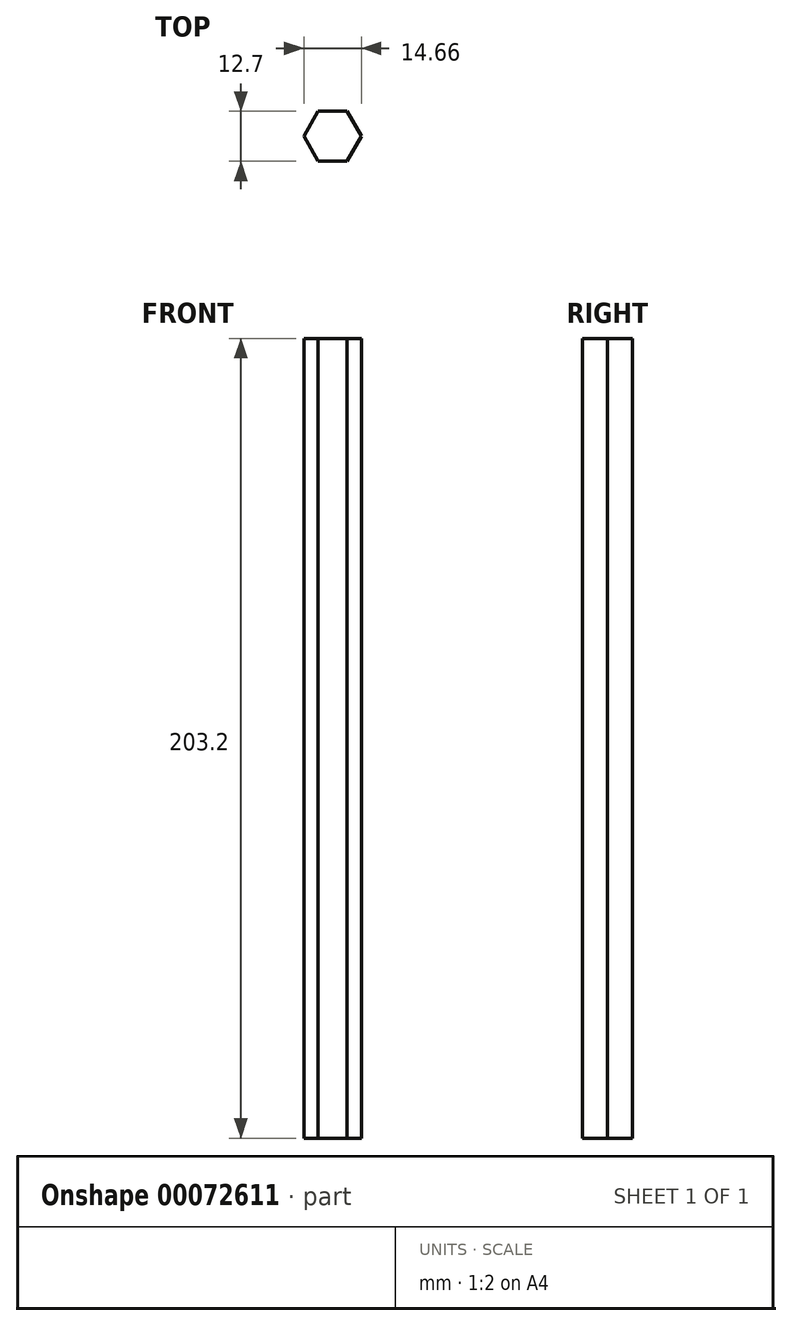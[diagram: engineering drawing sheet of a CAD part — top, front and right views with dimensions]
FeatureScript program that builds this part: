
annotation { "Feature Type Name" : "Feature", "Feature Type Description" : "" }
export const myFeature = defineFeature(function(context is Context, id is Id, definition is map)
    precondition{}
    {
        {
            var Q0;
            Q0=qCreatedBy(makeId("Top.planeOp"),FACE);
            var sketch = newSketch(context, id + "F0", { "sketchPlane" : qUnion([Q0])});
            skCircle(sketch, "E0.cCircle", {"center": v(0, 0) * mm, "radius": 6.35 * mm, "construction": true});
            skLineSegment(sketch, "E0.0", {"start": v(3.67, 6.35) * mm, "end": v(7.33, 0) * mm});
            skLineSegment(sketch, "E0.1", {"start": v(7.33, 0) * mm, "end": v(3.67, -6.35) * mm});
            skLineSegment(sketch, "E0.2", {"start": v(3.67, -6.35) * mm, "end": v(-3.67, -6.35) * mm});
            skLineSegment(sketch, "E0.3", {"start": v(-3.67, -6.35) * mm, "end": v(-7.33, 0) * mm});
            skLineSegment(sketch, "E0.4", {"start": v(-7.33, 0) * mm, "end": v(-3.67, 6.35) * mm});
            skLineSegment(sketch, "E0.5", {"start": v(-3.67, 6.35) * mm, "end": v(3.67, 6.35) * mm});
            skPoint(sketch, "E0.0.midPoint", {"position": v(5.5, 3.17) * mm});
            skSolve(sketch);
        }
        {
            var Q0;
            Q0=makeQuery(id+"F0.imprint","IMPRINT",FACE,{"disambiguationData":[TD([[makeQuery(id+"F0.imprint","IMPRINT",EDGE,{"derivedFrom":sQuery(id+"F0.wireOp",EDGE,"E0.0")}),-1.0]])]});
            extrude(context, id + "F1", {"entities" : qUnion([Q0]), "depth" : 203.2 * mm});
        }
    });
